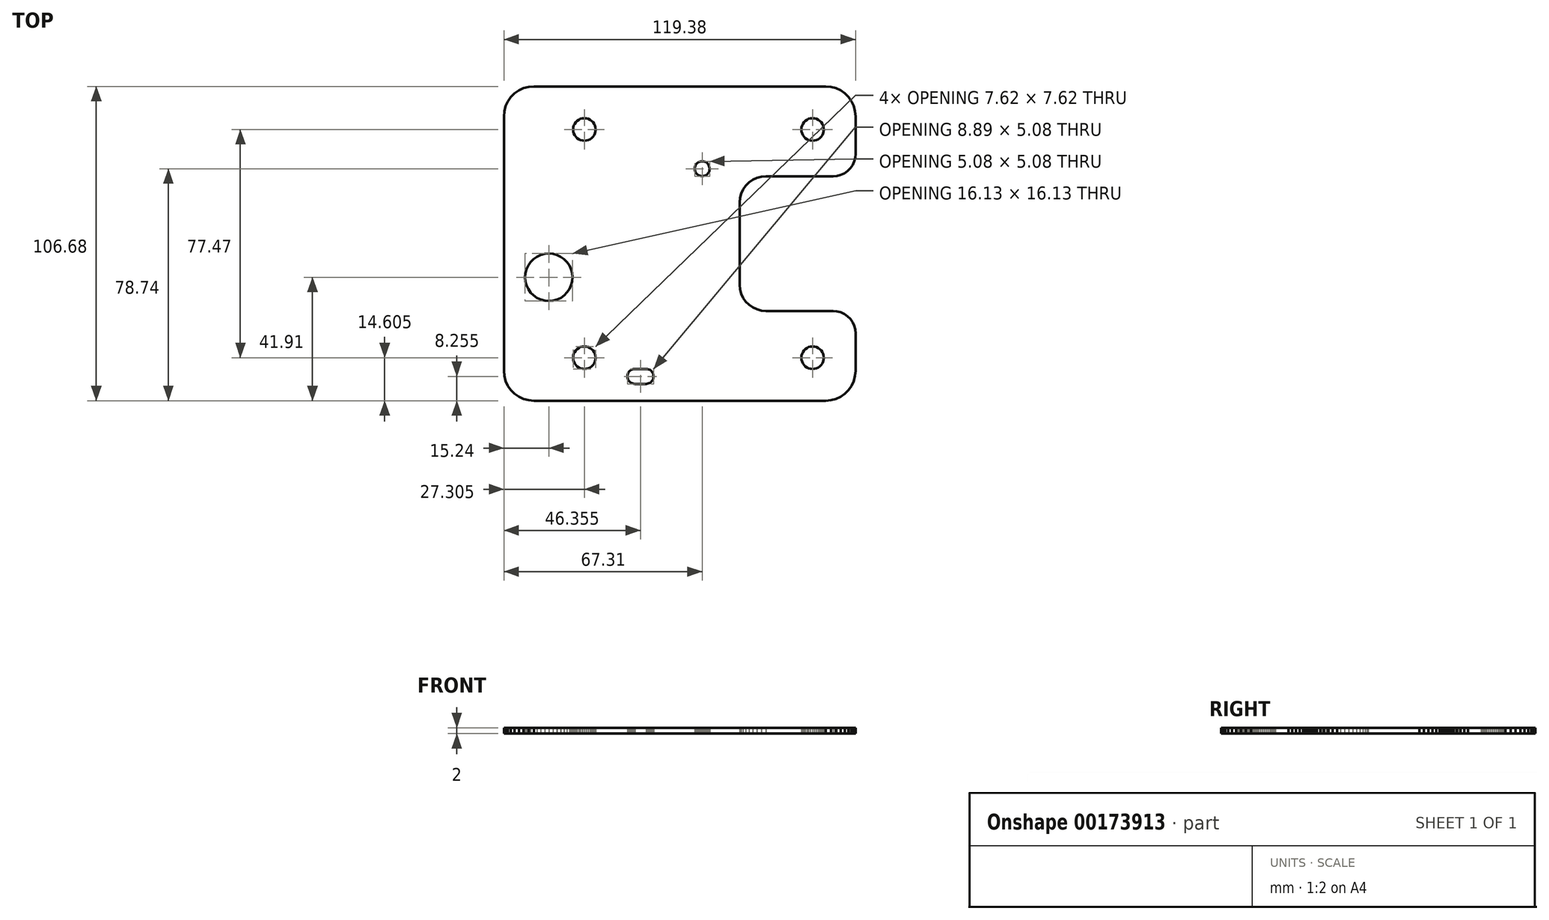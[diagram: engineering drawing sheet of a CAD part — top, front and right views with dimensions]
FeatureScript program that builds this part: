
annotation { "Feature Type Name" : "Feature", "Feature Type Description" : "" }
export const myFeature = defineFeature(function(context is Context, id is Id, definition is map)
    precondition{}
    {
        {
            var Q0;
            Q0=qCreatedBy(makeId("Top.planeOp"),FACE);
            var sketch = newSketch(context, id + "F0", { "sketchPlane" : qUnion([Q0])});
            skLineSegment(sketch, "E0", {"start": v(-9.04, 45.95) * mm, "end": v(-8.93, 45.53) * mm});
            skLineSegment(sketch, "E1", {"start": v(-17.78, 45.09) * mm, "end": v(-17.74, 45.53) * mm});
            skLineSegment(sketch, "E2", {"start": v(-8.93, 45.53) * mm, "end": v(-8.9, 45.09) * mm});
            skLineSegment(sketch, "E3", {"start": v(-8.9, 45.09) * mm, "end": v(-8.93, 44.64) * mm});
            skLineSegment(sketch, "E4", {"start": v(-11.43, 47.63) * mm, "end": v(-10.99, 47.59) * mm});
            skLineSegment(sketch, "E5", {"start": v(-17.19, 46.72) * mm, "end": v(-16.87, 47.03) * mm});
            skLineSegment(sketch, "E6", {"start": v(-16.51, 47.28) * mm, "end": v(-16.1, 47.47) * mm});
            skLineSegment(sketch, "E7", {"start": v(-15.68, 47.59) * mm, "end": v(-15.24, 47.63) * mm});
            skLineSegment(sketch, "E8", {"start": v(-8.93, 44.64) * mm, "end": v(-9.04, 44.22) * mm});
            skLineSegment(sketch, "E9", {"start": v(-10.56, 47.47) * mm, "end": v(-10.16, 47.28) * mm});
            skLineSegment(sketch, "E10", {"start": v(-17.74, 44.64) * mm, "end": v(-17.78, 45.09) * mm});
            skLineSegment(sketch, "E11", {"start": v(-16.1, 47.47) * mm, "end": v(-15.68, 47.59) * mm});
            skLineSegment(sketch, "E12", {"start": v(-15.24, 47.63) * mm, "end": v(-11.47, 47.63) * mm});
            skLineSegment(sketch, "E13", {"start": v(-10.99, 47.59) * mm, "end": v(-10.56, 47.47) * mm});
            skLineSegment(sketch, "E14", {"start": v(-9.23, 46.36) * mm, "end": v(-9.04, 45.95) * mm});
            skLineSegment(sketch, "E15", {"start": v(-17.63, 44.22) * mm, "end": v(-17.74, 44.64) * mm});
            skLineSegment(sketch, "E16", {"start": v(-17.74, 45.53) * mm, "end": v(-17.63, 45.95) * mm});
            skLineSegment(sketch, "E17", {"start": v(-17.44, 46.36) * mm, "end": v(-17.19, 46.72) * mm});
            skLineSegment(sketch, "E18", {"start": v(-16.87, 47.03) * mm, "end": v(-16.51, 47.28) * mm});
            skLineSegment(sketch, "E19", {"start": v(-11.47, 47.63) * mm, "end": v(-11.43, 47.63) * mm});
            skLineSegment(sketch, "E20", {"start": v(-10.16, 47.28) * mm, "end": v(-9.8, 47.03) * mm});
            skLineSegment(sketch, "E21", {"start": v(-17.63, 45.95) * mm, "end": v(-17.44, 46.36) * mm});
            skLineSegment(sketch, "E22", {"start": v(-9.8, 47.03) * mm, "end": v(-9.48, 46.72) * mm});
            skLineSegment(sketch, "E23", {"start": v(-9.48, 46.72) * mm, "end": v(-9.23, 46.36) * mm});
            skLineSegment(sketch, "E24", {"start": v(-45.86, -3.5) * mm, "end": v(-44.46, -3.37) * mm});
            skLineSegment(sketch, "E25", {"start": v(-49.64, -5.26) * mm, "end": v(-48.5, -4.45) * mm});
            skLineSegment(sketch, "E26", {"start": v(-44.46, -3.37) * mm, "end": v(-43.06, -3.49) * mm});
            skLineSegment(sketch, "E27", {"start": v(-45.84, -19.37) * mm, "end": v(-47.2, -19.01) * mm});
            skLineSegment(sketch, "E28", {"start": v(-48.5, -4.45) * mm, "end": v(-47.22, -3.86) * mm});
            skLineSegment(sketch, "E29", {"start": v(-50.62, -16.62) * mm, "end": v(-51.43, -15.47) * mm});
            skLineSegment(sketch, "E30", {"start": v(-51.43, -15.47) * mm, "end": v(-52.02, -14.2) * mm});
            skLineSegment(sketch, "E31", {"start": v(-52.02, -14.2) * mm, "end": v(-52.39, -12.84) * mm});
            skLineSegment(sketch, "E32", {"start": v(-52.03, -8.69) * mm, "end": v(-51.44, -7.41) * mm});
            skLineSegment(sketch, "E33", {"start": v(-52.39, -12.84) * mm, "end": v(-52.51, -11.44) * mm});
            skLineSegment(sketch, "E34", {"start": v(-52.51, -11.44) * mm, "end": v(-52.4, -10.04) * mm});
            skLineSegment(sketch, "E35", {"start": v(-37.47, -7.39) * mm, "end": v(-36.88, -8.66) * mm});
            skLineSegment(sketch, "E36", {"start": v(-36.5, -12.82) * mm, "end": v(-36.87, -14.17) * mm});
            skLineSegment(sketch, "E37", {"start": v(5.42, -24.13) * mm, "end": v(5.67, -23.77) * mm});
            skLineSegment(sketch, "E38", {"start": v(7.17, -22.9) * mm, "end": v(7.62, -22.86) * mm});
            skLineSegment(sketch, "E39", {"start": v(8.06, -22.9) * mm, "end": v(8.48, -23.01) * mm});
            skLineSegment(sketch, "E40", {"start": v(-37.46, -15.45) * mm, "end": v(-38.26, -16.6) * mm});
            skLineSegment(sketch, "E41", {"start": v(-39.26, -17.6) * mm, "end": v(-40.4, -18.4) * mm});
            skLineSegment(sketch, "E42", {"start": v(8.48, -23.01) * mm, "end": v(8.89, -23.2) * mm});
            skLineSegment(sketch, "E43", {"start": v(9.25, -23.45) * mm, "end": v(9.56, -23.76) * mm});
            skLineSegment(sketch, "E44", {"start": v(9.56, -23.76) * mm, "end": v(9.82, -24.13) * mm});
            skLineSegment(sketch, "E45", {"start": v(-39.28, -5.24) * mm, "end": v(-38.28, -6.24) * mm});
            skLineSegment(sketch, "E46", {"start": v(-17.44, 43.82) * mm, "end": v(-17.63, 44.22) * mm});
            skLineSegment(sketch, "E47", {"start": v(-51.44, -7.41) * mm, "end": v(-50.64, -6.26) * mm});
            skLineSegment(sketch, "E48", {"start": v(-10.99, 42.58) * mm, "end": v(-11.43, 42.55) * mm});
            skLineSegment(sketch, "E49", {"start": v(-40.43, -4.44) * mm, "end": v(-39.28, -5.24) * mm});
            skLineSegment(sketch, "E50", {"start": v(-49.62, -17.62) * mm, "end": v(-50.62, -16.62) * mm});
            skLineSegment(sketch, "E51", {"start": v(-15.68, 42.58) * mm, "end": v(-16.1, 42.7) * mm});
            skLineSegment(sketch, "E52", {"start": v(6.35, -23.2) * mm, "end": v(6.75, -23.02) * mm});
            skLineSegment(sketch, "E53", {"start": v(-36.88, -8.66) * mm, "end": v(-36.51, -10.02) * mm});
            skLineSegment(sketch, "E54", {"start": v(-43.04, -19.37) * mm, "end": v(-44.44, -19.5) * mm});
            skLineSegment(sketch, "E55", {"start": v(5.67, -23.77) * mm, "end": v(5.98, -23.46) * mm});
            skLineSegment(sketch, "E56", {"start": v(6.75, -23.02) * mm, "end": v(7.17, -22.9) * mm});
            skLineSegment(sketch, "E57", {"start": v(7.62, -22.86) * mm, "end": v(8.06, -22.9) * mm});
            skLineSegment(sketch, "E58", {"start": v(8.89, -23.2) * mm, "end": v(9.25, -23.45) * mm});
            skLineSegment(sketch, "E59", {"start": v(-48.47, -18.42) * mm, "end": v(-49.62, -17.62) * mm});
            skLineSegment(sketch, "E60", {"start": v(5.98, -23.46) * mm, "end": v(6.35, -23.2) * mm});
            skLineSegment(sketch, "E61", {"start": v(-15.24, 42.55) * mm, "end": v(-15.68, 42.58) * mm});
            skLineSegment(sketch, "E62", {"start": v(-16.87, 43.14) * mm, "end": v(-17.19, 43.45) * mm});
            skLineSegment(sketch, "E63", {"start": v(-9.48, 43.45) * mm, "end": v(-9.8, 43.14) * mm});
            skLineSegment(sketch, "E64", {"start": v(-17.19, 43.45) * mm, "end": v(-17.44, 43.82) * mm});
            skLineSegment(sketch, "E65", {"start": v(-9.23, 43.82) * mm, "end": v(-9.48, 43.45) * mm});
            skLineSegment(sketch, "E66", {"start": v(-15.2, 42.55) * mm, "end": v(-15.24, 42.55) * mm});
            skLineSegment(sketch, "E67", {"start": v(-16.1, 42.7) * mm, "end": v(-16.51, 42.89) * mm});
            skLineSegment(sketch, "E68", {"start": v(-43.06, -3.49) * mm, "end": v(-41.7, -3.85) * mm});
            skLineSegment(sketch, "E69", {"start": v(-38.28, -6.24) * mm, "end": v(-37.47, -7.39) * mm});
            skLineSegment(sketch, "E70", {"start": v(-11.43, 42.55) * mm, "end": v(-15.2, 42.55) * mm});
            skLineSegment(sketch, "E71", {"start": v(-16.51, 42.89) * mm, "end": v(-16.87, 43.14) * mm});
            skLineSegment(sketch, "E72", {"start": v(-47.22, -3.86) * mm, "end": v(-45.86, -3.5) * mm});
            skLineSegment(sketch, "E73", {"start": v(-36.39, -11.42) * mm, "end": v(-36.5, -12.82) * mm});
            skLineSegment(sketch, "E74", {"start": v(-36.87, -14.17) * mm, "end": v(-37.46, -15.45) * mm});
            skLineSegment(sketch, "E75", {"start": v(-9.04, 44.22) * mm, "end": v(-9.23, 43.82) * mm});
            skLineSegment(sketch, "E76", {"start": v(-50.64, -6.26) * mm, "end": v(-49.64, -5.26) * mm});
            skLineSegment(sketch, "E77", {"start": v(-41.7, -3.85) * mm, "end": v(-40.43, -4.44) * mm});
            skLineSegment(sketch, "E78", {"start": v(-36.51, -10.02) * mm, "end": v(-36.39, -11.42) * mm});
            skLineSegment(sketch, "E79", {"start": v(-10.16, 42.89) * mm, "end": v(-10.56, 42.7) * mm});
            skLineSegment(sketch, "E80", {"start": v(-38.26, -16.6) * mm, "end": v(-39.26, -17.6) * mm});
            skLineSegment(sketch, "E81", {"start": v(-9.8, 43.14) * mm, "end": v(-10.16, 42.89) * mm});
            skLineSegment(sketch, "E82", {"start": v(-40.4, -18.4) * mm, "end": v(-41.68, -19) * mm});
            skLineSegment(sketch, "E83", {"start": v(-41.68, -19) * mm, "end": v(-43.04, -19.37) * mm});
            skLineSegment(sketch, "E84", {"start": v(-44.44, -19.5) * mm, "end": v(-45.84, -19.37) * mm});
            skLineSegment(sketch, "E85", {"start": v(-47.2, -19.01) * mm, "end": v(-48.47, -18.42) * mm});
            skLineSegment(sketch, "E86", {"start": v(-10.56, 42.7) * mm, "end": v(-10.99, 42.58) * mm});
            skLineSegment(sketch, "E87", {"start": v(-52.4, -10.04) * mm, "end": v(-52.03, -8.69) * mm});
            skLineSegment(sketch, "E88", {"start": v(5.12, -24.96) * mm, "end": v(5.23, -24.54) * mm});
            skLineSegment(sketch, "E89", {"start": v(45.09, 42.55) * mm, "end": v(44.42, 42.49) * mm});
            skLineSegment(sketch, "E90", {"start": v(41.79, 36.83) * mm, "end": v(42.17, 36.29) * mm});
            skLineSegment(sketch, "E91", {"start": v(9.82, -26.67) * mm, "end": v(9.57, -27.03) * mm});
            skLineSegment(sketch, "E92", {"start": v(42.64, 41.65) * mm, "end": v(42.17, 41.18) * mm});
            skLineSegment(sketch, "E93", {"start": v(41.79, 40.64) * mm, "end": v(41.5, 40.04) * mm});
            skLineSegment(sketch, "E94", {"start": v(10.12, -24.95) * mm, "end": v(10.16, -25.4) * mm});
            skLineSegment(sketch, "E95", {"start": v(5.23, -24.54) * mm, "end": v(5.42, -24.13) * mm});
            skLineSegment(sketch, "E96", {"start": v(45.75, 34.98) * mm, "end": v(46.39, 35.15) * mm});
            skLineSegment(sketch, "E97", {"start": v(48.67, 40.04) * mm, "end": v(48.38, 40.64) * mm});
            skLineSegment(sketch, "E98", {"start": v(47.53, 41.65) * mm, "end": v(47, 42.03) * mm});
            skLineSegment(sketch, "E99", {"start": v(10, -26.26) * mm, "end": v(9.82, -26.67) * mm});
            skLineSegment(sketch, "E100", {"start": v(6.35, -27.6) * mm, "end": v(6, -27.35) * mm});
            skLineSegment(sketch, "E101", {"start": v(44.42, 42.49) * mm, "end": v(43.78, 42.32) * mm});
            skLineSegment(sketch, "E102", {"start": v(43.78, 42.32) * mm, "end": v(43.18, 42.03) * mm});
            skLineSegment(sketch, "E103", {"start": v(7.62, -27.94) * mm, "end": v(7.18, -27.9) * mm});
            skLineSegment(sketch, "E104", {"start": v(5.42, -26.67) * mm, "end": v(5.24, -26.27) * mm});
            skLineSegment(sketch, "E105", {"start": v(47, 42.03) * mm, "end": v(46.39, 42.32) * mm});
            skLineSegment(sketch, "E106", {"start": v(41.5, 37.43) * mm, "end": v(41.79, 36.83) * mm});
            skLineSegment(sketch, "E107", {"start": v(6.76, -27.79) * mm, "end": v(6.35, -27.6) * mm});
            skLineSegment(sketch, "E108", {"start": v(42.17, 36.29) * mm, "end": v(42.64, 35.82) * mm});
            skLineSegment(sketch, "E109", {"start": v(5.12, -25.85) * mm, "end": v(5.08, -25.4) * mm});
            skLineSegment(sketch, "E110", {"start": v(5.08, -25.4) * mm, "end": v(5.12, -24.96) * mm});
            skLineSegment(sketch, "E111", {"start": v(10.12, -25.84) * mm, "end": v(10, -26.26) * mm});
            skLineSegment(sketch, "E112", {"start": v(42.64, 35.82) * mm, "end": v(43.18, 35.44) * mm});
            skLineSegment(sketch, "E113", {"start": v(46.39, 35.15) * mm, "end": v(47, 35.44) * mm});
            skLineSegment(sketch, "E114", {"start": v(47, 35.44) * mm, "end": v(47.53, 35.82) * mm});
            skLineSegment(sketch, "E115", {"start": v(7.18, -27.9) * mm, "end": v(6.76, -27.79) * mm});
            skLineSegment(sketch, "E116", {"start": v(41.33, 39.4) * mm, "end": v(41.28, 38.73) * mm});
            skLineSegment(sketch, "E117", {"start": v(41.5, 40.04) * mm, "end": v(41.33, 39.4) * mm});
            skLineSegment(sketch, "E118", {"start": v(9.26, -27.34) * mm, "end": v(8.9, -27.6) * mm});
            skLineSegment(sketch, "E119", {"start": v(48.38, 40.64) * mm, "end": v(48, 41.18) * mm});
            skLineSegment(sketch, "E120", {"start": v(47.53, 35.82) * mm, "end": v(48, 36.29) * mm});
            skLineSegment(sketch, "E121", {"start": v(45.09, 34.93) * mm, "end": v(45.75, 34.98) * mm});
            skLineSegment(sketch, "E122", {"start": v(9.82, -24.13) * mm, "end": v(10, -24.53) * mm});
            skLineSegment(sketch, "E123", {"start": v(43.18, 35.44) * mm, "end": v(43.78, 35.15) * mm});
            skLineSegment(sketch, "E124", {"start": v(48.38, 36.83) * mm, "end": v(48.67, 37.43) * mm});
            skLineSegment(sketch, "E125", {"start": v(48, 41.18) * mm, "end": v(47.53, 41.65) * mm});
            skLineSegment(sketch, "E126", {"start": v(48.84, 38.07) * mm, "end": v(48.9, 38.73) * mm});
            skLineSegment(sketch, "E127", {"start": v(10.16, -25.4) * mm, "end": v(10.12, -25.84) * mm});
            skLineSegment(sketch, "E128", {"start": v(6, -27.35) * mm, "end": v(5.68, -27.04) * mm});
            skLineSegment(sketch, "E129", {"start": v(8.07, -27.9) * mm, "end": v(7.62, -27.94) * mm});
            skLineSegment(sketch, "E130", {"start": v(43.78, 35.15) * mm, "end": v(44.42, 34.98) * mm});
            skLineSegment(sketch, "E131", {"start": v(48, 36.29) * mm, "end": v(48.38, 36.83) * mm});
            skLineSegment(sketch, "E132", {"start": v(48.9, 38.73) * mm, "end": v(48.84, 39.4) * mm});
            skLineSegment(sketch, "E133", {"start": v(8.9, -27.6) * mm, "end": v(8.5, -27.78) * mm});
            skLineSegment(sketch, "E134", {"start": v(43.18, 42.03) * mm, "end": v(42.64, 41.65) * mm});
            skLineSegment(sketch, "E135", {"start": v(8.5, -27.78) * mm, "end": v(8.07, -27.9) * mm});
            skLineSegment(sketch, "E136", {"start": v(46.39, 42.32) * mm, "end": v(45.75, 42.49) * mm});
            skLineSegment(sketch, "E137", {"start": v(41.28, 38.73) * mm, "end": v(41.33, 38.07) * mm});
            skLineSegment(sketch, "E138", {"start": v(45.75, 42.49) * mm, "end": v(45.09, 42.55) * mm});
            skLineSegment(sketch, "E139", {"start": v(10, -24.53) * mm, "end": v(10.12, -24.95) * mm});
            skLineSegment(sketch, "E140", {"start": v(44.42, 34.98) * mm, "end": v(45.09, 34.93) * mm});
            skLineSegment(sketch, "E141", {"start": v(48.67, 37.43) * mm, "end": v(48.84, 38.07) * mm});
            skLineSegment(sketch, "E142", {"start": v(48.84, 39.4) * mm, "end": v(48.67, 40.04) * mm});
            skLineSegment(sketch, "E143", {"start": v(11.37, -0.65) * mm, "end": v(11.43, 0) * mm});
            skLineSegment(sketch, "E144", {"start": v(5.68, -27.04) * mm, "end": v(5.42, -26.67) * mm});
            skLineSegment(sketch, "E145", {"start": v(5.24, -26.27) * mm, "end": v(5.12, -25.85) * mm});
            skLineSegment(sketch, "E146", {"start": v(9.57, -27.03) * mm, "end": v(9.26, -27.34) * mm});
            skLineSegment(sketch, "E147", {"start": v(41.33, 38.07) * mm, "end": v(41.5, 37.43) * mm});
            skLineSegment(sketch, "E148", {"start": v(11.43, 0) * mm, "end": v(11.37, 0.66) * mm});
            skLineSegment(sketch, "E149", {"start": v(42.17, 41.18) * mm, "end": v(41.79, 40.64) * mm});
            skLineSegment(sketch, "E150", {"start": v(7.62, -3.8) * mm, "end": v(8.28, -3.75) * mm});
            skLineSegment(sketch, "E151", {"start": v(11.2, -1.3) * mm, "end": v(11.37, -0.66) * mm});
            skLineSegment(sketch, "E152", {"start": v(4.04, 1.3) * mm, "end": v(3.87, 0.66) * mm});
            skLineSegment(sketch, "E153", {"start": v(3.87, -0.66) * mm, "end": v(4.04, -1.3) * mm});
            skLineSegment(sketch, "E154", {"start": v(9.53, 3.3) * mm, "end": v(8.92, 3.58) * mm});
            skLineSegment(sketch, "E155", {"start": v(6.96, 3.75) * mm, "end": v(6.32, 3.58) * mm});
            skLineSegment(sketch, "E156", {"start": v(5.17, 2.92) * mm, "end": v(4.7, 2.45) * mm});
            skLineSegment(sketch, "E157", {"start": v(4.04, -1.3) * mm, "end": v(4.32, -1.9) * mm});
            skLineSegment(sketch, "E158", {"start": v(5.72, -3.3) * mm, "end": v(6.32, -3.58) * mm});
            skLineSegment(sketch, "E159", {"start": v(8.28, -3.75) * mm, "end": v(8.92, -3.58) * mm});
            skLineSegment(sketch, "E160", {"start": v(4.32, 1.9) * mm, "end": v(4.04, 1.3) * mm});
            skLineSegment(sketch, "E161", {"start": v(10.92, -1.9) * mm, "end": v(11.2, -1.3) * mm});
            skLineSegment(sketch, "E162", {"start": v(-35.3, -41.19) * mm, "end": v(-35.68, -40.65) * mm});
            skLineSegment(sketch, "E163", {"start": v(3.8, 0) * mm, "end": v(3.87, -0.66) * mm});
            skLineSegment(sketch, "E164", {"start": v(11.37, 0.66) * mm, "end": v(11.2, 1.3) * mm});
            skLineSegment(sketch, "E165", {"start": v(-35.68, -40.65) * mm, "end": v(-35.96, -40.04) * mm});
            skLineSegment(sketch, "E166", {"start": v(7.62, 3.8) * mm, "end": v(6.96, 3.75) * mm});
            skLineSegment(sketch, "E167", {"start": v(11.2, 1.3) * mm, "end": v(10.92, 1.9) * mm});
            skLineSegment(sketch, "E168", {"start": v(5.72, 3.3) * mm, "end": v(5.17, 2.92) * mm});
            skLineSegment(sketch, "E169", {"start": v(4.7, -2.45) * mm, "end": v(5.17, -2.92) * mm});
            skLineSegment(sketch, "E170", {"start": v(-34.83, -41.66) * mm, "end": v(-35.3, -41.19) * mm});
            skLineSegment(sketch, "E171", {"start": v(-36.2, -38.74) * mm, "end": v(-36.14, -38.08) * mm});
            skLineSegment(sketch, "E172", {"start": v(-36.14, -38.08) * mm, "end": v(-35.97, -37.44) * mm});
            skLineSegment(sketch, "E173", {"start": v(-35.97, -37.44) * mm, "end": v(-35.69, -36.84) * mm});
            skLineSegment(sketch, "E174", {"start": v(-35.3, -36.3) * mm, "end": v(-34.84, -35.82) * mm});
            skLineSegment(sketch, "E175", {"start": v(3.87, 0.66) * mm, "end": v(3.8, 0) * mm});
            skLineSegment(sketch, "E176", {"start": v(-33.05, -34.98) * mm, "end": v(-32.4, -34.93) * mm});
            skLineSegment(sketch, "E177", {"start": v(6.96, -3.75) * mm, "end": v(7.62, -3.8) * mm});
            skLineSegment(sketch, "E178", {"start": v(10.54, -2.45) * mm, "end": v(10.92, -1.9) * mm});
            skLineSegment(sketch, "E179", {"start": v(-31.73, -34.98) * mm, "end": v(-31.09, -35.15) * mm});
            skLineSegment(sketch, "E180", {"start": v(10.54, 2.45) * mm, "end": v(10.07, 2.92) * mm});
            skLineSegment(sketch, "E181", {"start": v(-33.7, -35.16) * mm, "end": v(-33.05, -34.98) * mm});
            skLineSegment(sketch, "E182", {"start": v(-31.09, -35.15) * mm, "end": v(-30.49, -35.43) * mm});
            skLineSegment(sketch, "E183", {"start": v(-35.96, -40.04) * mm, "end": v(-36.14, -39.4) * mm});
            skLineSegment(sketch, "E184", {"start": v(-30.49, -35.43) * mm, "end": v(-29.94, -35.81) * mm});
            skLineSegment(sketch, "E185", {"start": v(4.32, -1.9) * mm, "end": v(4.7, -2.45) * mm});
            skLineSegment(sketch, "E186", {"start": v(8.92, -3.58) * mm, "end": v(9.53, -3.3) * mm});
            skLineSegment(sketch, "E187", {"start": v(-29.94, -35.81) * mm, "end": v(-29.47, -36.28) * mm});
            skLineSegment(sketch, "E188", {"start": v(-29.47, -36.28) * mm, "end": v(-29.09, -36.82) * mm});
            skLineSegment(sketch, "E189", {"start": v(-34.3, -35.44) * mm, "end": v(-33.7, -35.16) * mm});
            skLineSegment(sketch, "E190", {"start": v(-29.09, -36.82) * mm, "end": v(-28.8, -37.43) * mm});
            skLineSegment(sketch, "E191", {"start": v(-36.14, -39.4) * mm, "end": v(-36.2, -38.74) * mm});
            skLineSegment(sketch, "E192", {"start": v(-28.63, -38.07) * mm, "end": v(-28.58, -38.73) * mm});
            skLineSegment(sketch, "E193", {"start": v(-28.58, -38.73) * mm, "end": v(-28.63, -39.39) * mm});
            skLineSegment(sketch, "E194", {"start": v(-28.63, -39.39) * mm, "end": v(-28.8, -40.03) * mm});
            skLineSegment(sketch, "E195", {"start": v(-32.4, -34.93) * mm, "end": v(-31.73, -34.98) * mm});
            skLineSegment(sketch, "E196", {"start": v(-28.8, -40.03) * mm, "end": v(-29.08, -40.63) * mm});
            skLineSegment(sketch, "E197", {"start": v(-34.84, -35.82) * mm, "end": v(-34.3, -35.44) * mm});
            skLineSegment(sketch, "E198", {"start": v(-29.08, -40.63) * mm, "end": v(-29.46, -41.18) * mm});
            skLineSegment(sketch, "E199", {"start": v(-29.46, -41.18) * mm, "end": v(-29.93, -41.65) * mm});
            skLineSegment(sketch, "E200", {"start": v(5.17, -2.92) * mm, "end": v(5.72, -3.3) * mm});
            skLineSegment(sketch, "E201", {"start": v(-29.93, -41.65) * mm, "end": v(-30.47, -42.03) * mm});
            skLineSegment(sketch, "E202", {"start": v(-30.47, -42.03) * mm, "end": v(-31.08, -42.31) * mm});
            skLineSegment(sketch, "E203", {"start": v(-28.8, -37.43) * mm, "end": v(-28.63, -38.07) * mm});
            skLineSegment(sketch, "E204", {"start": v(10.92, 1.9) * mm, "end": v(10.54, 2.45) * mm});
            skLineSegment(sketch, "E205", {"start": v(-35.69, -36.84) * mm, "end": v(-35.3, -36.3) * mm});
            skLineSegment(sketch, "E206", {"start": v(8.28, 3.75) * mm, "end": v(7.62, 3.8) * mm});
            skLineSegment(sketch, "E207", {"start": v(4.7, 2.45) * mm, "end": v(4.32, 1.9) * mm});
            skLineSegment(sketch, "E208", {"start": v(9.53, -3.3) * mm, "end": v(10.07, -2.92) * mm});
            skLineSegment(sketch, "E209", {"start": v(10.07, 2.92) * mm, "end": v(9.53, 3.3) * mm});
            skLineSegment(sketch, "E210", {"start": v(10.07, -2.92) * mm, "end": v(10.54, -2.45) * mm});
            skLineSegment(sketch, "E211", {"start": v(6.32, -3.58) * mm, "end": v(6.96, -3.75) * mm});
            skLineSegment(sketch, "E212", {"start": v(6.32, 3.58) * mm, "end": v(5.72, 3.3) * mm});
            skLineSegment(sketch, "E213", {"start": v(8.92, 3.58) * mm, "end": v(8.28, 3.75) * mm});
            skLineSegment(sketch, "E214", {"start": v(58.33, 48.26) * mm, "end": v(57.31, 49.71) * mm});
            skLineSegment(sketch, "E215", {"start": v(22.4, 19.68) * mm, "end": v(23.5, 20.78) * mm});
            skLineSegment(sketch, "E216", {"start": v(27.67, 22.72) * mm, "end": v(29.21, 22.86) * mm});
            skLineSegment(sketch, "E217", {"start": v(57.31, 49.71) * mm, "end": v(56.06, 50.96) * mm});
            skLineSegment(sketch, "E218", {"start": v(56.06, 50.96) * mm, "end": v(54.61, 51.98) * mm});
            skLineSegment(sketch, "E219", {"start": v(53.4, -22.98) * mm, "end": v(52.07, -22.86) * mm});
            skLineSegment(sketch, "E220", {"start": v(20.32, -13.97) * mm, "end": v(20.32, 13.7) * mm});
            skLineSegment(sketch, "E221", {"start": v(58.33, -48.26) * mm, "end": v(59.08, -46.65) * mm});
            skLineSegment(sketch, "E222", {"start": v(-32.38, -42.54) * mm, "end": v(-33.04, -42.49) * mm});
            skLineSegment(sketch, "E223", {"start": v(56.97, -24.64) * mm, "end": v(55.88, -23.88) * mm});
            skLineSegment(sketch, "E224", {"start": v(-34.28, -42.04) * mm, "end": v(-34.83, -41.66) * mm});
            skLineSegment(sketch, "E225", {"start": v(57.31, -49.71) * mm, "end": v(58.33, -48.26) * mm});
            skLineSegment(sketch, "E226", {"start": v(27.67, -22.72) * mm, "end": v(26.17, -22.32) * mm});
            skLineSegment(sketch, "E227", {"start": v(-33.68, -42.32) * mm, "end": v(-34.28, -42.04) * mm});
            skLineSegment(sketch, "E228", {"start": v(52.07, -22.86) * mm, "end": v(29.44, -22.86) * mm});
            skLineSegment(sketch, "E229", {"start": v(23.5, -20.78) * mm, "end": v(22.4, -19.68) * mm});
            skLineSegment(sketch, "E230", {"start": v(55.88, -23.88) * mm, "end": v(54.68, -23.32) * mm});
            skLineSegment(sketch, "E231", {"start": v(58.67, -26.67) * mm, "end": v(57.9, -25.58) * mm});
            skLineSegment(sketch, "E232", {"start": v(59.57, -29.16) * mm, "end": v(59.23, -27.87) * mm});
            skLineSegment(sketch, "E233", {"start": v(22.4, -19.68) * mm, "end": v(21.51, -18.42) * mm});
            skLineSegment(sketch, "E234", {"start": v(-31.08, -42.31) * mm, "end": v(-31.72, -42.49) * mm});
            skLineSegment(sketch, "E235", {"start": v(29.21, -22.86) * mm, "end": v(27.67, -22.72) * mm});
            skLineSegment(sketch, "E236", {"start": v(57.9, -25.58) * mm, "end": v(56.97, -24.64) * mm});
            skLineSegment(sketch, "E237", {"start": v(21.51, -18.42) * mm, "end": v(20.86, -17.01) * mm});
            skLineSegment(sketch, "E238", {"start": v(20.46, -15.51) * mm, "end": v(20.32, -13.97) * mm});
            skLineSegment(sketch, "E239", {"start": v(20.32, 13.97) * mm, "end": v(20.46, 15.51) * mm});
            skLineSegment(sketch, "E240", {"start": v(59.7, -30.48) * mm, "end": v(59.57, -29.16) * mm});
            skLineSegment(sketch, "E241", {"start": v(24.77, -21.67) * mm, "end": v(23.5, -20.78) * mm});
            skLineSegment(sketch, "E242", {"start": v(-31.72, -42.49) * mm, "end": v(-32.38, -42.54) * mm});
            skLineSegment(sketch, "E243", {"start": v(53.4, 22.98) * mm, "end": v(54.68, 23.32) * mm});
            skLineSegment(sketch, "E244", {"start": v(55.88, 23.88) * mm, "end": v(56.97, 24.64) * mm});
            skLineSegment(sketch, "E245", {"start": v(29.44, -22.86) * mm, "end": v(29.21, -22.86) * mm});
            skLineSegment(sketch, "E246", {"start": v(56.06, -50.96) * mm, "end": v(57.31, -49.71) * mm});
            skLineSegment(sketch, "E247", {"start": v(21.51, 18.42) * mm, "end": v(22.4, 19.68) * mm});
            skLineSegment(sketch, "E248", {"start": v(26.17, 22.32) * mm, "end": v(27.67, 22.72) * mm});
            skLineSegment(sketch, "E249", {"start": v(56.97, 24.64) * mm, "end": v(57.9, 25.58) * mm});
            skLineSegment(sketch, "E250", {"start": v(59.7, -30.6) * mm, "end": v(59.7, -30.48) * mm});
            skLineSegment(sketch, "E251", {"start": v(57.9, 25.58) * mm, "end": v(58.67, 26.67) * mm});
            skLineSegment(sketch, "E252", {"start": v(58.67, 26.67) * mm, "end": v(59.23, 27.87) * mm});
            skLineSegment(sketch, "E253", {"start": v(-33.04, -42.49) * mm, "end": v(-33.68, -42.32) * mm});
            skLineSegment(sketch, "E254", {"start": v(59.57, 29.16) * mm, "end": v(59.7, 30.48) * mm});
            skLineSegment(sketch, "E255", {"start": v(26.17, -22.32) * mm, "end": v(24.77, -21.67) * mm});
            skLineSegment(sketch, "E256", {"start": v(20.86, 17.01) * mm, "end": v(21.51, 18.42) * mm});
            skLineSegment(sketch, "E257", {"start": v(29.21, 22.86) * mm, "end": v(51.84, 22.86) * mm});
            skLineSegment(sketch, "E258", {"start": v(59.23, -27.87) * mm, "end": v(58.67, -26.67) * mm});
            skLineSegment(sketch, "E259", {"start": v(24.77, 21.67) * mm, "end": v(26.17, 22.32) * mm});
            skLineSegment(sketch, "E260", {"start": v(54.68, 23.32) * mm, "end": v(55.88, 23.88) * mm});
            skLineSegment(sketch, "E261", {"start": v(23.5, 20.78) * mm, "end": v(24.77, 21.67) * mm});
            skLineSegment(sketch, "E262", {"start": v(59.54, -44.94) * mm, "end": v(59.7, -43.18) * mm});
            skLineSegment(sketch, "E263", {"start": v(59.7, -43.18) * mm, "end": v(59.7, -30.6) * mm});
            skLineSegment(sketch, "E264", {"start": v(54.61, -51.98) * mm, "end": v(56.06, -50.96) * mm});
            skLineSegment(sketch, "E265", {"start": v(59.08, -46.65) * mm, "end": v(59.54, -44.94) * mm});
            skLineSegment(sketch, "E266", {"start": v(20.86, -17.01) * mm, "end": v(20.46, -15.51) * mm});
            skLineSegment(sketch, "E267", {"start": v(20.46, 15.51) * mm, "end": v(20.86, 17.01) * mm});
            skLineSegment(sketch, "E268", {"start": v(52.07, 22.86) * mm, "end": v(53.4, 22.98) * mm});
            skLineSegment(sketch, "E269", {"start": v(59.23, 27.87) * mm, "end": v(59.57, 29.16) * mm});
            skLineSegment(sketch, "E270", {"start": v(59.7, 30.48) * mm, "end": v(59.7, 43.05) * mm});
            skLineSegment(sketch, "E271", {"start": v(54.68, -23.32) * mm, "end": v(53.4, -22.98) * mm});
            skLineSegment(sketch, "E272", {"start": v(59.7, 43.05) * mm, "end": v(59.7, 43.18) * mm});
            skLineSegment(sketch, "E273", {"start": v(20.32, 13.7) * mm, "end": v(20.32, 13.97) * mm});
            skLineSegment(sketch, "E274", {"start": v(51.84, 22.86) * mm, "end": v(52.07, 22.86) * mm});
            skLineSegment(sketch, "E275", {"start": v(59.7, 43.18) * mm, "end": v(59.54, 44.94) * mm});
            skLineSegment(sketch, "E276", {"start": v(59.54, 44.94) * mm, "end": v(59.08, 46.65) * mm});
            skLineSegment(sketch, "E277", {"start": v(59.08, 46.65) * mm, "end": v(58.33, 48.26) * mm});
            skLineSegment(sketch, "E278", {"start": v(-59.08, -46.65) * mm, "end": v(-58.33, -48.26) * mm});
            skLineSegment(sketch, "E279", {"start": v(-54.61, -51.98) * mm, "end": v(-53, -52.73) * mm});
            skLineSegment(sketch, "E280", {"start": v(-49.53, -53.34) * mm, "end": v(-48.54, -53.34) * mm});
            skLineSegment(sketch, "E281", {"start": v(-48.54, -53.34) * mm, "end": v(49.53, -53.34) * mm});
            skLineSegment(sketch, "E282", {"start": v(-53, -52.73) * mm, "end": v(-51.3, -53.19) * mm});
            skLineSegment(sketch, "E283", {"start": v(-17.19, -43.45) * mm, "end": v(-16.87, -43.14) * mm});
            skLineSegment(sketch, "E284", {"start": v(-16.87, -43.14) * mm, "end": v(-16.51, -42.89) * mm});
            skLineSegment(sketch, "E285", {"start": v(-16.51, -42.89) * mm, "end": v(-16.1, -42.7) * mm});
            skLineSegment(sketch, "E286", {"start": v(-58.33, -48.26) * mm, "end": v(-57.31, -49.71) * mm});
            skLineSegment(sketch, "E287", {"start": v(-15.24, -42.55) * mm, "end": v(-11.47, -42.55) * mm});
            skLineSegment(sketch, "E288", {"start": v(-11.47, -42.55) * mm, "end": v(-11.43, -42.55) * mm});
            skLineSegment(sketch, "E289", {"start": v(-15.68, -47.59) * mm, "end": v(-16.1, -47.47) * mm});
            skLineSegment(sketch, "E290", {"start": v(-17.19, -46.72) * mm, "end": v(-17.44, -46.35) * mm});
            skLineSegment(sketch, "E291", {"start": v(-11.43, -42.55) * mm, "end": v(-10.99, -42.58) * mm});
            skLineSegment(sketch, "E292", {"start": v(-10.99, -42.58) * mm, "end": v(-10.56, -42.7) * mm});
            skLineSegment(sketch, "E293", {"start": v(-10.56, -42.7) * mm, "end": v(-10.16, -42.89) * mm});
            skLineSegment(sketch, "E294", {"start": v(-17.63, -45.95) * mm, "end": v(-17.74, -45.53) * mm});
            skLineSegment(sketch, "E295", {"start": v(-17.78, -45.09) * mm, "end": v(-17.74, -44.64) * mm});
            skLineSegment(sketch, "E296", {"start": v(-10.16, -42.89) * mm, "end": v(-9.8, -43.14) * mm});
            skLineSegment(sketch, "E297", {"start": v(-8.93, -44.64) * mm, "end": v(-8.9, -45.09) * mm});
            skLineSegment(sketch, "E298", {"start": v(-8.93, -45.53) * mm, "end": v(-9.04, -45.95) * mm});
            skLineSegment(sketch, "E299", {"start": v(-59.54, -44.94) * mm, "end": v(-59.08, -46.65) * mm});
            skLineSegment(sketch, "E300", {"start": v(-57.31, -49.71) * mm, "end": v(-56.06, -50.96) * mm});
            skLineSegment(sketch, "E301", {"start": v(-54.61, 51.98) * mm, "end": v(-56.06, 50.96) * mm});
            skLineSegment(sketch, "E302", {"start": v(53, -52.73) * mm, "end": v(54.61, -51.98) * mm});
            skLineSegment(sketch, "E303", {"start": v(-15.2, -47.63) * mm, "end": v(-15.24, -47.63) * mm});
            skLineSegment(sketch, "E304", {"start": v(-59.08, 46.65) * mm, "end": v(-59.54, 44.94) * mm});
            skLineSegment(sketch, "E305", {"start": v(-15.68, -42.58) * mm, "end": v(-15.24, -42.55) * mm});
            skLineSegment(sketch, "E306", {"start": v(-16.1, -47.47) * mm, "end": v(-16.51, -47.28) * mm});
            skLineSegment(sketch, "E307", {"start": v(-17.44, -43.82) * mm, "end": v(-17.19, -43.45) * mm});
            skLineSegment(sketch, "E308", {"start": v(-9.8, -43.14) * mm, "end": v(-9.48, -43.45) * mm});
            skLineSegment(sketch, "E309", {"start": v(-9.23, -43.82) * mm, "end": v(-9.04, -44.22) * mm});
            skLineSegment(sketch, "E310", {"start": v(-9.04, -44.22) * mm, "end": v(-8.93, -44.64) * mm});
            skLineSegment(sketch, "E311", {"start": v(-8.9, -45.09) * mm, "end": v(-8.93, -45.53) * mm});
            skLineSegment(sketch, "E312", {"start": v(-16.1, -42.7) * mm, "end": v(-15.68, -42.58) * mm});
            skLineSegment(sketch, "E313", {"start": v(-9.48, -43.45) * mm, "end": v(-9.23, -43.82) * mm});
            skLineSegment(sketch, "E314", {"start": v(-58.33, 48.26) * mm, "end": v(-59.08, 46.65) * mm});
            skLineSegment(sketch, "E315", {"start": v(-59.69, 42.32) * mm, "end": v(-59.69, -43.18) * mm});
            skLineSegment(sketch, "E316", {"start": v(48.54, 53.34) * mm, "end": v(-49.53, 53.34) * mm});
            skLineSegment(sketch, "E317", {"start": v(-59.69, -43.18) * mm, "end": v(-59.54, -44.94) * mm});
            skLineSegment(sketch, "E318", {"start": v(49.53, 53.34) * mm, "end": v(48.54, 53.34) * mm});
            skLineSegment(sketch, "E319", {"start": v(-57.31, 49.71) * mm, "end": v(-58.33, 48.26) * mm});
            skLineSegment(sketch, "E320", {"start": v(-59.54, 44.94) * mm, "end": v(-59.69, 43.18) * mm});
            skLineSegment(sketch, "E321", {"start": v(49.53, -53.34) * mm, "end": v(51.3, -53.19) * mm});
            skLineSegment(sketch, "E322", {"start": v(-15.24, -47.63) * mm, "end": v(-15.68, -47.59) * mm});
            skLineSegment(sketch, "E323", {"start": v(-56.06, 50.96) * mm, "end": v(-57.31, 49.71) * mm});
            skLineSegment(sketch, "E324", {"start": v(54.61, 51.98) * mm, "end": v(53, 52.73) * mm});
            skLineSegment(sketch, "E325", {"start": v(-59.69, 43.18) * mm, "end": v(-59.69, 42.32) * mm});
            skLineSegment(sketch, "E326", {"start": v(-51.3, -53.19) * mm, "end": v(-49.53, -53.34) * mm});
            skLineSegment(sketch, "E327", {"start": v(-16.87, -47.03) * mm, "end": v(-17.19, -46.72) * mm});
            skLineSegment(sketch, "E328", {"start": v(51.3, 53.19) * mm, "end": v(49.53, 53.34) * mm});
            skLineSegment(sketch, "E329", {"start": v(-56.06, -50.96) * mm, "end": v(-54.61, -51.98) * mm});
            skLineSegment(sketch, "E330", {"start": v(53, 52.73) * mm, "end": v(51.3, 53.19) * mm});
            skLineSegment(sketch, "E331", {"start": v(51.3, -53.19) * mm, "end": v(53, -52.73) * mm});
            skLineSegment(sketch, "E332", {"start": v(-51.3, 53.19) * mm, "end": v(-53, 52.73) * mm});
            skLineSegment(sketch, "E333", {"start": v(-16.51, -47.28) * mm, "end": v(-16.87, -47.03) * mm});
            skLineSegment(sketch, "E334", {"start": v(-49.53, 53.34) * mm, "end": v(-51.3, 53.19) * mm});
            skLineSegment(sketch, "E335", {"start": v(-17.44, -46.35) * mm, "end": v(-17.63, -45.95) * mm});
            skLineSegment(sketch, "E336", {"start": v(-17.74, -45.53) * mm, "end": v(-17.78, -45.09) * mm});
            skLineSegment(sketch, "E337", {"start": v(-17.74, -44.64) * mm, "end": v(-17.63, -44.22) * mm});
            skLineSegment(sketch, "E338", {"start": v(-17.63, -44.22) * mm, "end": v(-17.44, -43.82) * mm});
            skLineSegment(sketch, "E339", {"start": v(-53, 52.73) * mm, "end": v(-54.61, 51.98) * mm});
            skLineSegment(sketch, "E340", {"start": v(-28.63, 39.4) * mm, "end": v(-28.58, 38.74) * mm});
            skLineSegment(sketch, "E341", {"start": v(-31.72, 34.98) * mm, "end": v(-32.38, 34.93) * mm});
            skLineSegment(sketch, "E342", {"start": v(5.23, 26.26) * mm, "end": v(5.42, 26.67) * mm});
            skLineSegment(sketch, "E343", {"start": v(-36.14, 39.39) * mm, "end": v(-35.97, 40.03) * mm});
            skLineSegment(sketch, "E344", {"start": v(-34.28, 35.43) * mm, "end": v(-34.83, 35.81) * mm});
            skLineSegment(sketch, "E345", {"start": v(-35.3, 36.28) * mm, "end": v(-35.68, 36.82) * mm});
            skLineSegment(sketch, "E346", {"start": v(-10.99, -47.59) * mm, "end": v(-11.43, -47.63) * mm});
            skLineSegment(sketch, "E347", {"start": v(-28.58, 38.74) * mm, "end": v(-28.63, 38.08) * mm});
            skLineSegment(sketch, "E348", {"start": v(7.62, 27.94) * mm, "end": v(8.06, 27.9) * mm});
            skLineSegment(sketch, "E349", {"start": v(8.06, 27.9) * mm, "end": v(8.48, 27.79) * mm});
            skLineSegment(sketch, "E350", {"start": v(-28.63, 38.08) * mm, "end": v(-28.8, 37.44) * mm});
            skLineSegment(sketch, "E351", {"start": v(-29.46, 36.3) * mm, "end": v(-29.93, 35.82) * mm});
            skLineSegment(sketch, "E352", {"start": v(-36.2, 38.73) * mm, "end": v(-36.14, 39.39) * mm});
            skLineSegment(sketch, "E353", {"start": v(-31.73, 42.49) * mm, "end": v(-31.09, 42.32) * mm});
            skLineSegment(sketch, "E354", {"start": v(-32.38, 34.93) * mm, "end": v(-33.04, 34.98) * mm});
            skLineSegment(sketch, "E355", {"start": v(-33.04, 34.98) * mm, "end": v(-33.68, 35.15) * mm});
            skLineSegment(sketch, "E356", {"start": v(-9.8, -47.03) * mm, "end": v(-10.16, -47.28) * mm});
            skLineSegment(sketch, "E357", {"start": v(-33.7, 42.31) * mm, "end": v(-33.05, 42.49) * mm});
            skLineSegment(sketch, "E358", {"start": v(-29.94, 41.66) * mm, "end": v(-29.47, 41.19) * mm});
            skLineSegment(sketch, "E359", {"start": v(-29.93, 35.82) * mm, "end": v(-30.47, 35.44) * mm});
            skLineSegment(sketch, "E360", {"start": v(-32.4, 42.54) * mm, "end": v(-31.73, 42.49) * mm});
            skLineSegment(sketch, "E361", {"start": v(5.12, 25.84) * mm, "end": v(5.23, 26.26) * mm});
            skLineSegment(sketch, "E362", {"start": v(-29.09, 40.65) * mm, "end": v(-28.8, 40.04) * mm});
            skLineSegment(sketch, "E363", {"start": v(-28.8, 40.04) * mm, "end": v(-28.63, 39.4) * mm});
            skLineSegment(sketch, "E364", {"start": v(-36.14, 38.07) * mm, "end": v(-36.2, 38.73) * mm});
            skLineSegment(sketch, "E365", {"start": v(5.42, 26.67) * mm, "end": v(5.67, 27.03) * mm});
            skLineSegment(sketch, "E366", {"start": v(5.67, 27.03) * mm, "end": v(5.98, 27.34) * mm});
            skLineSegment(sketch, "E367", {"start": v(-9.23, -46.35) * mm, "end": v(-9.48, -46.72) * mm});
            skLineSegment(sketch, "E368", {"start": v(-33.05, 42.49) * mm, "end": v(-32.4, 42.54) * mm});
            skLineSegment(sketch, "E369", {"start": v(-35.96, 37.43) * mm, "end": v(-36.14, 38.07) * mm});
            skLineSegment(sketch, "E370", {"start": v(-35.68, 36.82) * mm, "end": v(-35.96, 37.43) * mm});
            skLineSegment(sketch, "E371", {"start": v(-35.69, 40.63) * mm, "end": v(-35.3, 41.18) * mm});
            skLineSegment(sketch, "E372", {"start": v(-28.8, 37.44) * mm, "end": v(-29.08, 36.84) * mm});
            skLineSegment(sketch, "E373", {"start": v(8.48, 27.79) * mm, "end": v(8.89, 27.6) * mm});
            skLineSegment(sketch, "E374", {"start": v(7.17, 27.9) * mm, "end": v(7.62, 27.94) * mm});
            skLineSegment(sketch, "E375", {"start": v(-10.16, -47.28) * mm, "end": v(-10.56, -47.47) * mm});
            skLineSegment(sketch, "E376", {"start": v(5.98, 27.34) * mm, "end": v(6.35, 27.6) * mm});
            skLineSegment(sketch, "E377", {"start": v(8.89, 27.6) * mm, "end": v(9.25, 27.35) * mm});
            skLineSegment(sketch, "E378", {"start": v(-29.08, 36.84) * mm, "end": v(-29.46, 36.3) * mm});
            skLineSegment(sketch, "E379", {"start": v(9.56, 27.04) * mm, "end": v(9.82, 26.67) * mm});
            skLineSegment(sketch, "E380", {"start": v(-11.43, -47.63) * mm, "end": v(-15.2, -47.63) * mm});
            skLineSegment(sketch, "E381", {"start": v(-31.09, 42.32) * mm, "end": v(-30.49, 42.04) * mm});
            skLineSegment(sketch, "E382", {"start": v(-34.3, 42.03) * mm, "end": v(-33.7, 42.31) * mm});
            skLineSegment(sketch, "E383", {"start": v(6.35, 27.6) * mm, "end": v(6.75, 27.78) * mm});
            skLineSegment(sketch, "E384", {"start": v(9.25, 27.35) * mm, "end": v(9.56, 27.04) * mm});
            skLineSegment(sketch, "E385", {"start": v(10, 26.27) * mm, "end": v(10.12, 25.85) * mm});
            skLineSegment(sketch, "E386", {"start": v(-9.04, -45.95) * mm, "end": v(-9.23, -46.35) * mm});
            skLineSegment(sketch, "E387", {"start": v(-35.3, 41.18) * mm, "end": v(-34.84, 41.65) * mm});
            skLineSegment(sketch, "E388", {"start": v(-34.84, 41.65) * mm, "end": v(-34.3, 42.03) * mm});
            skLineSegment(sketch, "E389", {"start": v(-30.47, 35.44) * mm, "end": v(-31.08, 35.16) * mm});
            skLineSegment(sketch, "E390", {"start": v(-33.68, 35.15) * mm, "end": v(-34.28, 35.43) * mm});
            skLineSegment(sketch, "E391", {"start": v(-31.08, 35.16) * mm, "end": v(-31.72, 34.98) * mm});
            skLineSegment(sketch, "E392", {"start": v(-10.56, -47.47) * mm, "end": v(-10.99, -47.59) * mm});
            skLineSegment(sketch, "E393", {"start": v(5.12, 24.95) * mm, "end": v(5.08, 25.4) * mm});
            skLineSegment(sketch, "E394", {"start": v(6.75, 27.78) * mm, "end": v(7.17, 27.9) * mm});
            skLineSegment(sketch, "E395", {"start": v(9.82, 26.67) * mm, "end": v(10, 26.27) * mm});
            skLineSegment(sketch, "E396", {"start": v(10.12, 25.85) * mm, "end": v(10.16, 25.4) * mm});
            skLineSegment(sketch, "E397", {"start": v(10.16, 25.4) * mm, "end": v(10.12, 24.96) * mm});
            skLineSegment(sketch, "E398", {"start": v(-30.49, 42.04) * mm, "end": v(-29.94, 41.66) * mm});
            skLineSegment(sketch, "E399", {"start": v(-29.47, 41.19) * mm, "end": v(-29.09, 40.65) * mm});
            skLineSegment(sketch, "E400", {"start": v(-35.97, 40.03) * mm, "end": v(-35.69, 40.63) * mm});
            skLineSegment(sketch, "E401", {"start": v(-9.48, -46.72) * mm, "end": v(-9.8, -47.03) * mm});
            skLineSegment(sketch, "E402", {"start": v(5.08, 25.4) * mm, "end": v(5.12, 25.84) * mm});
            skLineSegment(sketch, "E403", {"start": v(-34.83, 35.81) * mm, "end": v(-35.3, 36.28) * mm});
            skLineSegment(sketch, "E404", {"start": v(10.12, 24.96) * mm, "end": v(10, 24.54) * mm});
            skLineSegment(sketch, "E405", {"start": v(46.38, -35.15) * mm, "end": v(46.98, -35.43) * mm});
            skLineSegment(sketch, "E406", {"start": v(41.28, -38.74) * mm, "end": v(41.33, -38.08) * mm});
            skLineSegment(sketch, "E407", {"start": v(41.78, -36.84) * mm, "end": v(42.16, -36.3) * mm});
            skLineSegment(sketch, "E408", {"start": v(8.07, 22.9) * mm, "end": v(7.62, 22.86) * mm});
            skLineSegment(sketch, "E409", {"start": v(6.35, 23.2) * mm, "end": v(6, 23.45) * mm});
            skLineSegment(sketch, "E410", {"start": v(5.42, 24.13) * mm, "end": v(5.24, 24.53) * mm});
            skLineSegment(sketch, "E411", {"start": v(42.16, -36.3) * mm, "end": v(42.63, -35.82) * mm});
            skLineSegment(sketch, "E412", {"start": v(44.42, -34.98) * mm, "end": v(45.08, -34.93) * mm});
            skLineSegment(sketch, "E413", {"start": v(46.98, -35.43) * mm, "end": v(47.53, -35.81) * mm});
            skLineSegment(sketch, "E414", {"start": v(41.33, -39.4) * mm, "end": v(41.28, -38.74) * mm});
            skLineSegment(sketch, "E415", {"start": v(48.84, -38.07) * mm, "end": v(48.9, -38.73) * mm});
            skLineSegment(sketch, "E416", {"start": v(48.9, -38.73) * mm, "end": v(48.84, -39.39) * mm});
            skLineSegment(sketch, "E417", {"start": v(41.5, -37.44) * mm, "end": v(41.78, -36.84) * mm});
            skLineSegment(sketch, "E418", {"start": v(9.82, 24.13) * mm, "end": v(9.57, 23.77) * mm});
            skLineSegment(sketch, "E419", {"start": v(48.67, -40.03) * mm, "end": v(48.39, -40.63) * mm});
            skLineSegment(sketch, "E420", {"start": v(6.76, 23.01) * mm, "end": v(6.35, 23.2) * mm});
            skLineSegment(sketch, "E421", {"start": v(9.57, 23.77) * mm, "end": v(9.26, 23.46) * mm});
            skLineSegment(sketch, "E422", {"start": v(5.68, 23.76) * mm, "end": v(5.42, 24.13) * mm});
            skLineSegment(sketch, "E423", {"start": v(43.17, -35.44) * mm, "end": v(43.78, -35.16) * mm});
            skLineSegment(sketch, "E424", {"start": v(48.84, -39.39) * mm, "end": v(48.67, -40.03) * mm});
            skLineSegment(sketch, "E425", {"start": v(48.39, -40.63) * mm, "end": v(48, -41.18) * mm});
            skLineSegment(sketch, "E426", {"start": v(47, -42.03) * mm, "end": v(46.4, -42.31) * mm});
            skLineSegment(sketch, "E427", {"start": v(46.4, -42.31) * mm, "end": v(45.75, -42.49) * mm});
            skLineSegment(sketch, "E428", {"start": v(45.75, -42.49) * mm, "end": v(45.1, -42.54) * mm});
            skLineSegment(sketch, "E429", {"start": v(41.33, -38.08) * mm, "end": v(41.5, -37.44) * mm});
            skLineSegment(sketch, "E430", {"start": v(44.43, -42.49) * mm, "end": v(43.79, -42.32) * mm});
            skLineSegment(sketch, "E431", {"start": v(45.74, -34.98) * mm, "end": v(46.38, -35.15) * mm});
            skLineSegment(sketch, "E432", {"start": v(48.66, -37.43) * mm, "end": v(48.84, -38.07) * mm});
            skLineSegment(sketch, "E433", {"start": v(42.17, -41.19) * mm, "end": v(41.79, -40.65) * mm});
            skLineSegment(sketch, "E434", {"start": v(8.9, 23.2) * mm, "end": v(8.5, 23.02) * mm});
            skLineSegment(sketch, "E435", {"start": v(42.64, -41.66) * mm, "end": v(42.17, -41.19) * mm});
            skLineSegment(sketch, "E436", {"start": v(41.5, -40.04) * mm, "end": v(41.33, -39.4) * mm});
            skLineSegment(sketch, "E437", {"start": v(48, -41.18) * mm, "end": v(47.54, -41.65) * mm});
            skLineSegment(sketch, "E438", {"start": v(10, 24.54) * mm, "end": v(9.82, 24.13) * mm});
            skLineSegment(sketch, "E439", {"start": v(42.63, -35.82) * mm, "end": v(43.17, -35.44) * mm});
            skLineSegment(sketch, "E440", {"start": v(47.53, -35.81) * mm, "end": v(48, -36.28) * mm});
            skLineSegment(sketch, "E441", {"start": v(43.19, -42.04) * mm, "end": v(42.64, -41.66) * mm});
            skLineSegment(sketch, "E442", {"start": v(47.54, -41.65) * mm, "end": v(47, -42.03) * mm});
            skLineSegment(sketch, "E443", {"start": v(41.79, -40.65) * mm, "end": v(41.5, -40.04) * mm});
            skLineSegment(sketch, "E444", {"start": v(43.79, -42.32) * mm, "end": v(43.19, -42.04) * mm});
            skLineSegment(sketch, "E445", {"start": v(43.78, -35.16) * mm, "end": v(44.42, -34.98) * mm});
            skLineSegment(sketch, "E446", {"start": v(9.26, 23.46) * mm, "end": v(8.9, 23.2) * mm});
            skLineSegment(sketch, "E447", {"start": v(45.1, -42.54) * mm, "end": v(44.43, -42.49) * mm});
            skLineSegment(sketch, "E448", {"start": v(7.18, 22.9) * mm, "end": v(6.76, 23.01) * mm});
            skLineSegment(sketch, "E449", {"start": v(5.24, 24.53) * mm, "end": v(5.12, 24.95) * mm});
            skLineSegment(sketch, "E450", {"start": v(48, -36.28) * mm, "end": v(48.38, -36.82) * mm});
            skLineSegment(sketch, "E451", {"start": v(8.5, 23.02) * mm, "end": v(8.07, 22.9) * mm});
            skLineSegment(sketch, "E452", {"start": v(48.38, -36.82) * mm, "end": v(48.66, -37.43) * mm});
            skLineSegment(sketch, "E453", {"start": v(45.08, -34.93) * mm, "end": v(45.74, -34.98) * mm});
            skLineSegment(sketch, "E454", {"start": v(6, 23.45) * mm, "end": v(5.68, 23.76) * mm});
            skLineSegment(sketch, "E455", {"start": v(7.62, 22.86) * mm, "end": v(7.18, 22.9) * mm});
            skSolve(sketch);
        }
        {
            var Q0;
            Q0 = qSketchRegion(id + "F0", true);
            extrude(context, id + "F1", {"entities" : qUnion([Q0]), "depth" : 2 * mm});
        }
    });
